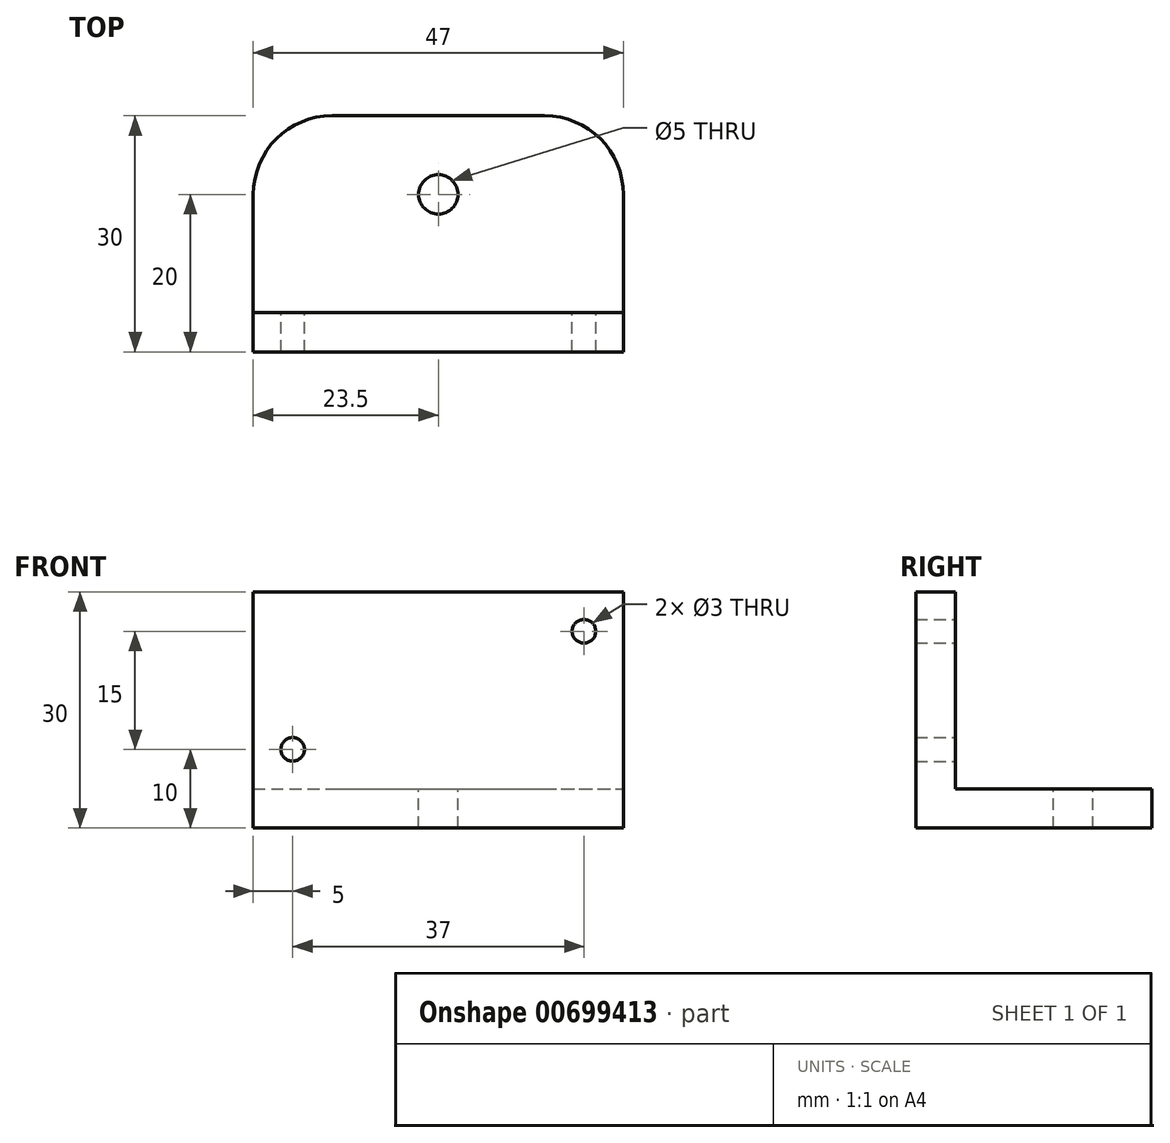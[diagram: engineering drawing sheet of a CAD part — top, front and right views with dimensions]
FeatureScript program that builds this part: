
annotation { "Feature Type Name" : "Feature", "Feature Type Description" : "" }
export const myFeature = defineFeature(function(context is Context, id is Id, definition is map)
    precondition{}
    {
        {
            var Q0;
            Q0=qCreatedBy(makeId("Front.planeOp"),FACE);
            var sketch = newSketch(context, id + "F0", { "sketchPlane" : qUnion([Q0])});
            skLineSegment(sketch, "E0.bottom", {"start": v(-23.5, 12.5) * mm, "end": v(23.5, 12.5) * mm});
            skLineSegment(sketch, "E0.top", {"start": v(-23.5, -12.5) * mm, "end": v(23.5, -12.5) * mm});
            skLineSegment(sketch, "E0.left", {"start": v(-23.5, 12.5) * mm, "end": v(-23.5, -12.5) * mm});
            skLineSegment(sketch, "E0.right", {"start": v(23.5, 12.5) * mm, "end": v(23.5, -12.5) * mm});
            skPoint(sketch, "E0.middle", {"position": v(0, 0) * mm});
            skCircle(sketch, "E1", {"center": v(-18.5, -7.5) * mm, "radius": 1.5 * mm});
            skCircle(sketch, "E2", {"center": v(18.5, 7.5) * mm, "radius": 1.5 * mm});
            skSolve(sketch);
        }
        {
            var Q0;
            Q0=makeQuery(id+"F0.imprint","IMPRINT",FACE,{"disambiguationData":[TD([[makeQuery(id+"F0.imprint","IMPRINT",EDGE,{"derivedFrom":sQuery(id+"F0.wireOp",EDGE,"E0.bottom")}),-1.0]])]});
            extrude(context, id + "F1", {"entities" : qUnion([Q0]), "depth" : 5 * mm, "offsetDistance" : 25 * mm});
        }
        {
            var Q0;
            Q0=makeQuery(id+"F1.opExtrude","SWEPT_FACE",FACE,{"disambiguationData":[OSD([sQuery(id+"F0.wireOp",EDGE,"E0.top")])]});
            var sketch = newSketch(context, id + "F2", { "sketchPlane" : qUnion([Q0])});
            skLineSegment(sketch, "E3.bottom", {"start": v(-23.5, 5) * mm, "end": v(23.5, 5) * mm});
            skLineSegment(sketch, "E3.top", {"start": v(-13.5, -25) * mm, "end": v(13.5, -25) * mm});
            skLineSegment(sketch, "E3.left", {"start": v(-23.5, 5) * mm, "end": v(-23.5, -15) * mm});
            skLineSegment(sketch, "E3.right", {"start": v(23.5, 5) * mm, "end": v(23.5, -15) * mm});
            skPoint(sketch, "E4.visualSharp", {"position": v(-23.5, -25) * mm});
            skArc(sketch, "E4.filletArc", {"start": v(-23.5, -15) * mm, "mid": v(-20.57, -22.07) * mm, "end": v(-13.5, -25) * mm});
            skPoint(sketch, "E5.visualSharp", {"position": v(23.5, -25) * mm});
            skArc(sketch, "E5.filletArc", {"start": v(13.5, -25) * mm, "mid": v(20.57, -22.07) * mm, "end": v(23.5, -15) * mm});
            skCircle(sketch, "E6", {"center": v(0, -15) * mm, "radius": 2.5 * mm});
            skSolve(sketch);
        }
        {
            var Q0;
            Q0=makeQuery(id+"F2.imprint","IMPRINT",FACE,{"disambiguationData":[TD([[makeQuery(id+"F2.imprint","IMPRINT",EDGE,{"derivedFrom":sQuery(id+"F2.wireOp",EDGE,"E3.top")}),1.0]])]});
            var Q1;
            {var subQ0=sQuery(id+"F2.wireOp",EDGE,"E3.bottom");Q1=makeQuery(id+"F2.imprint","IMPRINT",FACE,{"disambiguationData":[TD([[makeQuery(id+"F2.imprint","IMPRINT",EDGE,{"derivedFrom":subQ0}),-1.0]])]});}
            extrude(context, id + "F3", {"entities" : qUnion([Q0, Q1]), "operationType" : NewBodyOperationType.ADD, "depth" : 5 * mm, "offsetDistance" : 25 * mm});
        }
    });
